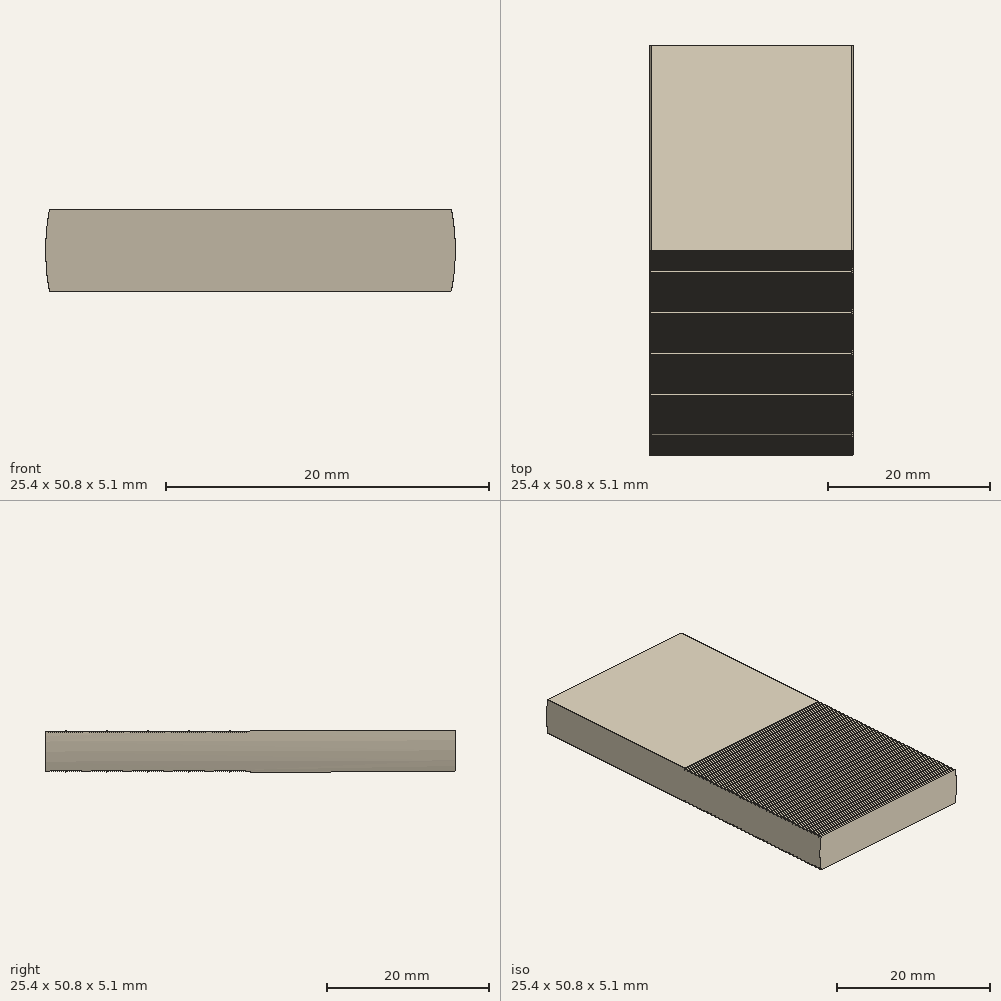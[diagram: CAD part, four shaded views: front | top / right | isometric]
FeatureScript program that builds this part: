
annotation { "Feature Type Name" : "Feature", "Feature Type Description" : "" }
export const myFeature = defineFeature(function(context is Context, id is Id, definition is map)
    precondition{}
    {
        {
            var Q0;
            Q0=qCreatedBy(makeId("Front.planeOp"),FACE);
            var sketch = newSketch(context, id + "F0", { "sketchPlane" : qUnion([Q0])});
            skCircle(sketch, "E0", {"center": v(0, 0) * mm, "radius": 12.7 * mm});
            skSolve(sketch);
        }
        {
            var Q0;
            Q0 = qSketchRegion(id + "F0", true);
            extrude(context, id + "F1", {"entities" : qUnion([Q0]), "endBound" : BoundingType.SYMMETRIC, "depth" : 50.8 * mm, "offsetDistance" : 25.4 * mm});
        }
        {
            var Q0;
            Q0=makeQuery(id+"F1.opExtrude","CAP_FACE",FACE,{"disambiguationData":[OSD([sQuery(id+"F0.wireOp",EDGE,"E0")])],"isStart":false});
            var sketch = newSketch(context, id + "F2", { "sketchPlane" : qUnion([Q0])});
            skLineSegment(sketch, "E1.bottom", {"start": v(12.45, 2.54) * mm, "end": v(-12.45, 2.54) * mm});
            skLineSegment(sketch, "E1.top", {"start": v(12.45, -2.54) * mm, "end": v(-12.45, -2.54) * mm});
            skPoint(sketch, "E1.middle", {"position": v(0, 0) * mm});
            skArc(sketch, "E2", {"start": v(-12.45, 2.54) * mm, "mid": v(-12.7, 0) * mm, "end": v(-12.45, -2.54) * mm});
            skArc(sketch, "E3.trimOffspring", {"start": v(12.45, -2.54) * mm, "mid": v(12.7, 0) * mm, "end": v(12.45, 2.54) * mm});
            skSolve(sketch);
        }
        {
            var Q0;
            Q0 = qSketchRegion(id + "F2", true);
            extrude(context, id + "F3", {"entities" : qUnion([Q0]), "operationType" : NewBodyOperationType.INTERSECT, "oppositeDirection" : true, "depth" : 50.8 * mm, "offsetDistance" : 25.4 * mm});
        }
        {
            var Q0;
            Q0=qCreatedBy(makeId("Right.planeOp"),FACE);
            var sketch = newSketch(context, id + "F4", { "sketchPlane" : qUnion([Q0])});
            skLineSegment(sketch, "E4", {"start": v(0, 2.54) * mm, "end": v(-0.13, 2.32) * mm});
            skLineSegment(sketch, "E5", {"start": v(-0.13, 2.32) * mm, "end": v(-0.25, 2.54) * mm});
            skLineSegment(sketch, "E6.1.0.0", {"start": v(-0.25, 2.54) * mm, "end": v(-0.38, 2.32) * mm});
            skLineSegment(sketch, "E6.1.0.1", {"start": v(-0.38, 2.32) * mm, "end": v(-0.5, 2.54) * mm});
            skLineSegment(sketch, "E6.2.0.0", {"start": v(-0.5, 2.54) * mm, "end": v(-0.64, 2.32) * mm});
            skLineSegment(sketch, "E6.2.0.1", {"start": v(-0.64, 2.32) * mm, "end": v(-0.76, 2.54) * mm});
            skLineSegment(sketch, "E6.3.0.0", {"start": v(-0.76, 2.54) * mm, "end": v(-0.89, 2.32) * mm});
            skLineSegment(sketch, "E6.3.0.1", {"start": v(-0.89, 2.32) * mm, "end": v(-1.02, 2.54) * mm});
            skLineSegment(sketch, "E6.4.0.0", {"start": v(-1.02, 2.54) * mm, "end": v(-1.14, 2.32) * mm});
            skLineSegment(sketch, "E6.4.0.1", {"start": v(-1.14, 2.32) * mm, "end": v(-1.27, 2.54) * mm});
            skLineSegment(sketch, "E6.5.0.0", {"start": v(-1.27, 2.54) * mm, "end": v(-1.4, 2.32) * mm});
            skLineSegment(sketch, "E6.5.0.1", {"start": v(-1.4, 2.32) * mm, "end": v(-1.52, 2.54) * mm});
            skLineSegment(sketch, "E6.6.0.0", {"start": v(-1.52, 2.54) * mm, "end": v(-1.65, 2.32) * mm});
            skLineSegment(sketch, "E6.6.0.1", {"start": v(-1.65, 2.32) * mm, "end": v(-1.78, 2.54) * mm});
            skLineSegment(sketch, "E6.7.0.0", {"start": v(-1.78, 2.54) * mm, "end": v(-1.9, 2.32) * mm});
            skLineSegment(sketch, "E6.7.0.1", {"start": v(-1.9, 2.32) * mm, "end": v(-2.03, 2.54) * mm});
            skLineSegment(sketch, "E6.8.0.0", {"start": v(-2.03, 2.54) * mm, "end": v(-2.16, 2.32) * mm});
            skLineSegment(sketch, "E6.8.0.1", {"start": v(-2.16, 2.32) * mm, "end": v(-2.29, 2.54) * mm});
            skLineSegment(sketch, "E6.9.0.0", {"start": v(-2.29, 2.54) * mm, "end": v(-2.41, 2.32) * mm});
            skLineSegment(sketch, "E6.9.0.1", {"start": v(-2.41, 2.32) * mm, "end": v(-2.54, 2.54) * mm});
            skLineSegment(sketch, "E6.10.0.0", {"start": v(-2.54, 2.54) * mm, "end": v(-2.67, 2.32) * mm});
            skLineSegment(sketch, "E6.10.0.1", {"start": v(-2.67, 2.32) * mm, "end": v(-2.8, 2.54) * mm});
            skLineSegment(sketch, "E6.11.0.0", {"start": v(-2.8, 2.54) * mm, "end": v(-2.92, 2.32) * mm});
            skLineSegment(sketch, "E6.11.0.1", {"start": v(-2.92, 2.32) * mm, "end": v(-3.05, 2.54) * mm});
            skLineSegment(sketch, "E6.12.0.0", {"start": v(-3.05, 2.54) * mm, "end": v(-3.18, 2.32) * mm});
            skLineSegment(sketch, "E6.12.0.1", {"start": v(-3.18, 2.32) * mm, "end": v(-3.3, 2.54) * mm});
            skLineSegment(sketch, "E6.13.0.0", {"start": v(-3.3, 2.54) * mm, "end": v(-3.43, 2.32) * mm});
            skLineSegment(sketch, "E6.13.0.1", {"start": v(-3.43, 2.32) * mm, "end": v(-3.56, 2.54) * mm});
            skLineSegment(sketch, "E6.14.0.0", {"start": v(-3.56, 2.54) * mm, "end": v(-3.68, 2.32) * mm});
            skLineSegment(sketch, "E6.14.0.1", {"start": v(-3.68, 2.32) * mm, "end": v(-3.81, 2.54) * mm});
            skLineSegment(sketch, "E6.15.0.0", {"start": v(-3.81, 2.54) * mm, "end": v(-3.94, 2.32) * mm});
            skLineSegment(sketch, "E6.15.0.1", {"start": v(-3.94, 2.32) * mm, "end": v(-4.06, 2.54) * mm});
            skLineSegment(sketch, "E6.16.0.0", {"start": v(-4.06, 2.54) * mm, "end": v(-4.2, 2.32) * mm});
            skLineSegment(sketch, "E6.16.0.1", {"start": v(-4.2, 2.32) * mm, "end": v(-4.32, 2.54) * mm});
            skLineSegment(sketch, "E6.17.0.0", {"start": v(-4.32, 2.54) * mm, "end": v(-4.45, 2.32) * mm});
            skLineSegment(sketch, "E6.17.0.1", {"start": v(-4.45, 2.32) * mm, "end": v(-4.57, 2.54) * mm});
            skLineSegment(sketch, "E6.18.0.0", {"start": v(-4.57, 2.54) * mm, "end": v(-4.7, 2.32) * mm});
            skLineSegment(sketch, "E6.18.0.1", {"start": v(-4.7, 2.32) * mm, "end": v(-4.83, 2.54) * mm});
            skLineSegment(sketch, "E6.19.0.0", {"start": v(-4.83, 2.54) * mm, "end": v(-4.95, 2.32) * mm});
            skLineSegment(sketch, "E6.19.0.1", {"start": v(-4.95, 2.32) * mm, "end": v(-5.08, 2.54) * mm});
            skLineSegment(sketch, "E6.20.0.0", {"start": v(-5.08, 2.54) * mm, "end": v(-5.2, 2.32) * mm});
            skLineSegment(sketch, "E6.20.0.1", {"start": v(-5.2, 2.32) * mm, "end": v(-5.33, 2.54) * mm});
            skLineSegment(sketch, "E6.21.0.0", {"start": v(-5.33, 2.54) * mm, "end": v(-5.46, 2.32) * mm});
            skLineSegment(sketch, "E6.21.0.1", {"start": v(-5.46, 2.32) * mm, "end": v(-5.59, 2.54) * mm});
            skLineSegment(sketch, "E6.22.0.0", {"start": v(-5.59, 2.54) * mm, "end": v(-5.72, 2.32) * mm});
            skLineSegment(sketch, "E6.22.0.1", {"start": v(-5.72, 2.32) * mm, "end": v(-5.84, 2.54) * mm});
            skLineSegment(sketch, "E6.23.0.0", {"start": v(-5.84, 2.54) * mm, "end": v(-5.97, 2.32) * mm});
            skLineSegment(sketch, "E6.23.0.1", {"start": v(-5.97, 2.32) * mm, "end": v(-6.1, 2.54) * mm});
            skLineSegment(sketch, "E6.24.0.0", {"start": v(-6.1, 2.54) * mm, "end": v(-6.22, 2.32) * mm});
            skLineSegment(sketch, "E6.24.0.1", {"start": v(-6.22, 2.32) * mm, "end": v(-6.35, 2.54) * mm});
            skLineSegment(sketch, "E6.25.0.0", {"start": v(-6.35, 2.54) * mm, "end": v(-6.48, 2.32) * mm});
            skLineSegment(sketch, "E6.25.0.1", {"start": v(-6.48, 2.32) * mm, "end": v(-6.6, 2.54) * mm});
            skLineSegment(sketch, "E6.26.0.0", {"start": v(-6.6, 2.54) * mm, "end": v(-6.73, 2.32) * mm});
            skLineSegment(sketch, "E6.26.0.1", {"start": v(-6.73, 2.32) * mm, "end": v(-6.86, 2.54) * mm});
            skLineSegment(sketch, "E6.27.0.0", {"start": v(-6.86, 2.54) * mm, "end": v(-6.99, 2.32) * mm});
            skLineSegment(sketch, "E6.27.0.1", {"start": v(-6.99, 2.32) * mm, "end": v(-7.11, 2.54) * mm});
            skLineSegment(sketch, "E6.28.0.0", {"start": v(-7.11, 2.54) * mm, "end": v(-7.24, 2.32) * mm});
            skLineSegment(sketch, "E6.28.0.1", {"start": v(-7.24, 2.32) * mm, "end": v(-7.37, 2.54) * mm});
            skLineSegment(sketch, "E6.29.0.0", {"start": v(-7.37, 2.54) * mm, "end": v(-7.5, 2.32) * mm});
            skLineSegment(sketch, "E6.29.0.1", {"start": v(-7.5, 2.32) * mm, "end": v(-7.62, 2.54) * mm});
            skLineSegment(sketch, "E6.30.0.0", {"start": v(-7.62, 2.54) * mm, "end": v(-7.75, 2.32) * mm});
            skLineSegment(sketch, "E6.30.0.1", {"start": v(-7.75, 2.32) * mm, "end": v(-7.87, 2.54) * mm});
            skLineSegment(sketch, "E6.31.0.0", {"start": v(-7.87, 2.54) * mm, "end": v(-8, 2.32) * mm});
            skLineSegment(sketch, "E6.31.0.1", {"start": v(-8, 2.32) * mm, "end": v(-8.13, 2.54) * mm});
            skLineSegment(sketch, "E6.32.0.0", {"start": v(-8.13, 2.54) * mm, "end": v(-8.26, 2.32) * mm});
            skLineSegment(sketch, "E6.32.0.1", {"start": v(-8.26, 2.32) * mm, "end": v(-8.38, 2.54) * mm});
            skLineSegment(sketch, "E6.33.0.0", {"start": v(-8.38, 2.54) * mm, "end": v(-8.5, 2.32) * mm});
            skLineSegment(sketch, "E6.33.0.1", {"start": v(-8.5, 2.32) * mm, "end": v(-8.64, 2.54) * mm});
            skLineSegment(sketch, "E6.34.0.0", {"start": v(-8.64, 2.54) * mm, "end": v(-8.76, 2.32) * mm});
            skLineSegment(sketch, "E6.34.0.1", {"start": v(-8.76, 2.32) * mm, "end": v(-8.9, 2.54) * mm});
            skLineSegment(sketch, "E6.35.0.0", {"start": v(-8.9, 2.54) * mm, "end": v(-9.02, 2.32) * mm});
            skLineSegment(sketch, "E6.35.0.1", {"start": v(-9.02, 2.32) * mm, "end": v(-9.14, 2.54) * mm});
            skLineSegment(sketch, "E6.36.0.0", {"start": v(-9.14, 2.54) * mm, "end": v(-9.27, 2.32) * mm});
            skLineSegment(sketch, "E6.36.0.1", {"start": v(-9.27, 2.32) * mm, "end": v(-9.4, 2.54) * mm});
            skLineSegment(sketch, "E6.37.0.0", {"start": v(-9.4, 2.54) * mm, "end": v(-9.53, 2.32) * mm});
            skLineSegment(sketch, "E6.37.0.1", {"start": v(-9.53, 2.32) * mm, "end": v(-9.65, 2.54) * mm});
            skLineSegment(sketch, "E6.38.0.0", {"start": v(-9.65, 2.54) * mm, "end": v(-9.78, 2.32) * mm});
            skLineSegment(sketch, "E6.38.0.1", {"start": v(-9.78, 2.32) * mm, "end": v(-9.9, 2.54) * mm});
            skLineSegment(sketch, "E6.39.0.0", {"start": v(-9.9, 2.54) * mm, "end": v(-10.03, 2.32) * mm});
            skLineSegment(sketch, "E6.39.0.1", {"start": v(-10.03, 2.32) * mm, "end": v(-10.16, 2.54) * mm});
            skLineSegment(sketch, "E6.40.0.0", {"start": v(-10.16, 2.54) * mm, "end": v(-10.29, 2.32) * mm});
            skLineSegment(sketch, "E6.40.0.1", {"start": v(-10.29, 2.32) * mm, "end": v(-10.41, 2.54) * mm});
            skLineSegment(sketch, "E6.41.0.0", {"start": v(-10.41, 2.54) * mm, "end": v(-10.54, 2.32) * mm});
            skLineSegment(sketch, "E6.41.0.1", {"start": v(-10.54, 2.32) * mm, "end": v(-10.67, 2.54) * mm});
            skLineSegment(sketch, "E6.42.0.0", {"start": v(-10.67, 2.54) * mm, "end": v(-10.8, 2.32) * mm});
            skLineSegment(sketch, "E6.42.0.1", {"start": v(-10.8, 2.32) * mm, "end": v(-10.92, 2.54) * mm});
            skLineSegment(sketch, "E6.43.0.0", {"start": v(-10.92, 2.54) * mm, "end": v(-11.05, 2.32) * mm});
            skLineSegment(sketch, "E6.43.0.1", {"start": v(-11.05, 2.32) * mm, "end": v(-11.18, 2.54) * mm});
            skLineSegment(sketch, "E6.44.0.0", {"start": v(-11.18, 2.54) * mm, "end": v(-11.3, 2.32) * mm});
            skLineSegment(sketch, "E6.44.0.1", {"start": v(-11.3, 2.32) * mm, "end": v(-11.43, 2.54) * mm});
            skLineSegment(sketch, "E6.45.0.0", {"start": v(-11.43, 2.54) * mm, "end": v(-11.56, 2.32) * mm});
            skLineSegment(sketch, "E6.45.0.1", {"start": v(-11.56, 2.32) * mm, "end": v(-11.68, 2.54) * mm});
            skLineSegment(sketch, "E6.46.0.0", {"start": v(-11.68, 2.54) * mm, "end": v(-11.81, 2.32) * mm});
            skLineSegment(sketch, "E6.46.0.1", {"start": v(-11.81, 2.32) * mm, "end": v(-11.94, 2.54) * mm});
            skLineSegment(sketch, "E6.47.0.0", {"start": v(-11.94, 2.54) * mm, "end": v(-12.07, 2.32) * mm});
            skLineSegment(sketch, "E6.47.0.1", {"start": v(-12.07, 2.32) * mm, "end": v(-12.2, 2.54) * mm});
            skLineSegment(sketch, "E6.48.0.0", {"start": v(-12.2, 2.54) * mm, "end": v(-12.32, 2.32) * mm});
            skLineSegment(sketch, "E6.48.0.1", {"start": v(-12.32, 2.32) * mm, "end": v(-12.45, 2.54) * mm});
            skLineSegment(sketch, "E6.49.0.0", {"start": v(-12.45, 2.54) * mm, "end": v(-12.57, 2.32) * mm});
            skLineSegment(sketch, "E6.49.0.1", {"start": v(-12.57, 2.32) * mm, "end": v(-12.7, 2.54) * mm});
            skLineSegment(sketch, "E6.50.0.0", {"start": v(-12.7, 2.54) * mm, "end": v(-12.83, 2.32) * mm});
            skLineSegment(sketch, "E6.50.0.1", {"start": v(-12.83, 2.32) * mm, "end": v(-12.95, 2.54) * mm});
            skLineSegment(sketch, "E6.51.0.0", {"start": v(-12.95, 2.54) * mm, "end": v(-13.08, 2.32) * mm});
            skLineSegment(sketch, "E6.51.0.1", {"start": v(-13.08, 2.32) * mm, "end": v(-13.2, 2.54) * mm});
            skLineSegment(sketch, "E6.52.0.0", {"start": v(-13.2, 2.54) * mm, "end": v(-13.34, 2.32) * mm});
            skLineSegment(sketch, "E6.52.0.1", {"start": v(-13.34, 2.32) * mm, "end": v(-13.46, 2.54) * mm});
            skLineSegment(sketch, "E6.53.0.0", {"start": v(-13.46, 2.54) * mm, "end": v(-13.59, 2.32) * mm});
            skLineSegment(sketch, "E6.53.0.1", {"start": v(-13.59, 2.32) * mm, "end": v(-13.72, 2.54) * mm});
            skLineSegment(sketch, "E6.54.0.0", {"start": v(-13.72, 2.54) * mm, "end": v(-13.84, 2.32) * mm});
            skLineSegment(sketch, "E6.54.0.1", {"start": v(-13.84, 2.32) * mm, "end": v(-13.97, 2.54) * mm});
            skLineSegment(sketch, "E6.55.0.0", {"start": v(-13.97, 2.54) * mm, "end": v(-14.1, 2.32) * mm});
            skLineSegment(sketch, "E6.55.0.1", {"start": v(-14.1, 2.32) * mm, "end": v(-14.22, 2.54) * mm});
            skLineSegment(sketch, "E6.56.0.0", {"start": v(-14.22, 2.54) * mm, "end": v(-14.35, 2.32) * mm});
            skLineSegment(sketch, "E6.56.0.1", {"start": v(-14.35, 2.32) * mm, "end": v(-14.48, 2.54) * mm});
            skLineSegment(sketch, "E6.57.0.0", {"start": v(-14.48, 2.54) * mm, "end": v(-14.6, 2.32) * mm});
            skLineSegment(sketch, "E6.57.0.1", {"start": v(-14.6, 2.32) * mm, "end": v(-14.73, 2.54) * mm});
            skLineSegment(sketch, "E6.58.0.0", {"start": v(-14.73, 2.54) * mm, "end": v(-14.86, 2.32) * mm});
            skLineSegment(sketch, "E6.58.0.1", {"start": v(-14.86, 2.32) * mm, "end": v(-14.99, 2.54) * mm});
            skLineSegment(sketch, "E6.59.0.0", {"start": v(-14.99, 2.54) * mm, "end": v(-15.11, 2.32) * mm});
            skLineSegment(sketch, "E6.59.0.1", {"start": v(-15.11, 2.32) * mm, "end": v(-15.24, 2.54) * mm});
            skLineSegment(sketch, "E6.60.0.0", {"start": v(-15.24, 2.54) * mm, "end": v(-15.37, 2.32) * mm});
            skLineSegment(sketch, "E6.60.0.1", {"start": v(-15.37, 2.32) * mm, "end": v(-15.5, 2.54) * mm});
            skLineSegment(sketch, "E6.61.0.0", {"start": v(-15.5, 2.54) * mm, "end": v(-15.62, 2.32) * mm});
            skLineSegment(sketch, "E6.61.0.1", {"start": v(-15.62, 2.32) * mm, "end": v(-15.75, 2.54) * mm});
            skLineSegment(sketch, "E6.62.0.0", {"start": v(-15.75, 2.54) * mm, "end": v(-15.88, 2.32) * mm});
            skLineSegment(sketch, "E6.62.0.1", {"start": v(-15.88, 2.32) * mm, "end": v(-16, 2.54) * mm});
            skLineSegment(sketch, "E6.63.0.0", {"start": v(-16, 2.54) * mm, "end": v(-16.13, 2.32) * mm});
            skLineSegment(sketch, "E6.63.0.1", {"start": v(-16.13, 2.32) * mm, "end": v(-16.26, 2.54) * mm});
            skLineSegment(sketch, "E6.64.0.0", {"start": v(-16.26, 2.54) * mm, "end": v(-16.38, 2.32) * mm});
            skLineSegment(sketch, "E6.64.0.1", {"start": v(-16.38, 2.32) * mm, "end": v(-16.51, 2.54) * mm});
            skLineSegment(sketch, "E6.65.0.0", {"start": v(-16.51, 2.54) * mm, "end": v(-16.64, 2.32) * mm});
            skLineSegment(sketch, "E6.65.0.1", {"start": v(-16.64, 2.32) * mm, "end": v(-16.76, 2.54) * mm});
            skLineSegment(sketch, "E6.66.0.0", {"start": v(-16.76, 2.54) * mm, "end": v(-16.9, 2.32) * mm});
            skLineSegment(sketch, "E6.66.0.1", {"start": v(-16.9, 2.32) * mm, "end": v(-17.02, 2.54) * mm});
            skLineSegment(sketch, "E6.67.0.0", {"start": v(-17.02, 2.54) * mm, "end": v(-17.15, 2.32) * mm});
            skLineSegment(sketch, "E6.67.0.1", {"start": v(-17.15, 2.32) * mm, "end": v(-17.27, 2.54) * mm});
            skLineSegment(sketch, "E6.68.0.0", {"start": v(-17.27, 2.54) * mm, "end": v(-17.4, 2.32) * mm});
            skLineSegment(sketch, "E6.68.0.1", {"start": v(-17.4, 2.32) * mm, "end": v(-17.53, 2.54) * mm});
            skLineSegment(sketch, "E6.69.0.0", {"start": v(-17.53, 2.54) * mm, "end": v(-17.65, 2.32) * mm});
            skLineSegment(sketch, "E6.69.0.1", {"start": v(-17.65, 2.32) * mm, "end": v(-17.78, 2.54) * mm});
            skLineSegment(sketch, "E6.70.0.0", {"start": v(-17.78, 2.54) * mm, "end": v(-17.9, 2.32) * mm});
            skLineSegment(sketch, "E6.70.0.1", {"start": v(-17.9, 2.32) * mm, "end": v(-18.03, 2.54) * mm});
            skLineSegment(sketch, "E6.71.0.0", {"start": v(-18.03, 2.54) * mm, "end": v(-18.16, 2.32) * mm});
            skLineSegment(sketch, "E6.71.0.1", {"start": v(-18.16, 2.32) * mm, "end": v(-18.29, 2.54) * mm});
            skLineSegment(sketch, "E6.72.0.0", {"start": v(-18.29, 2.54) * mm, "end": v(-18.42, 2.32) * mm});
            skLineSegment(sketch, "E6.72.0.1", {"start": v(-18.42, 2.32) * mm, "end": v(-18.54, 2.54) * mm});
            skLineSegment(sketch, "E6.73.0.0", {"start": v(-18.54, 2.54) * mm, "end": v(-18.67, 2.32) * mm});
            skLineSegment(sketch, "E6.73.0.1", {"start": v(-18.67, 2.32) * mm, "end": v(-18.8, 2.54) * mm});
            skLineSegment(sketch, "E6.74.0.0", {"start": v(-18.8, 2.54) * mm, "end": v(-18.92, 2.32) * mm});
            skLineSegment(sketch, "E6.74.0.1", {"start": v(-18.92, 2.32) * mm, "end": v(-19.05, 2.54) * mm});
            skLineSegment(sketch, "E6.75.0.0", {"start": v(-19.05, 2.54) * mm, "end": v(-19.18, 2.32) * mm});
            skLineSegment(sketch, "E6.75.0.1", {"start": v(-19.18, 2.32) * mm, "end": v(-19.3, 2.54) * mm});
            skLineSegment(sketch, "E6.76.0.0", {"start": v(-19.3, 2.54) * mm, "end": v(-19.43, 2.32) * mm});
            skLineSegment(sketch, "E6.76.0.1", {"start": v(-19.43, 2.32) * mm, "end": v(-19.56, 2.54) * mm});
            skLineSegment(sketch, "E6.77.0.0", {"start": v(-19.56, 2.54) * mm, "end": v(-19.69, 2.32) * mm});
            skLineSegment(sketch, "E6.77.0.1", {"start": v(-19.69, 2.32) * mm, "end": v(-19.81, 2.54) * mm});
            skLineSegment(sketch, "E6.78.0.0", {"start": v(-19.81, 2.54) * mm, "end": v(-19.94, 2.32) * mm});
            skLineSegment(sketch, "E6.78.0.1", {"start": v(-19.94, 2.32) * mm, "end": v(-20.07, 2.54) * mm});
            skLineSegment(sketch, "E6.79.0.0", {"start": v(-20.07, 2.54) * mm, "end": v(-20.2, 2.32) * mm});
            skLineSegment(sketch, "E6.79.0.1", {"start": v(-20.2, 2.32) * mm, "end": v(-20.32, 2.54) * mm});
            skLineSegment(sketch, "E6.80.0.0", {"start": v(-20.32, 2.54) * mm, "end": v(-20.45, 2.32) * mm});
            skLineSegment(sketch, "E6.80.0.1", {"start": v(-20.45, 2.32) * mm, "end": v(-20.57, 2.54) * mm});
            skLineSegment(sketch, "E6.81.0.0", {"start": v(-20.57, 2.54) * mm, "end": v(-20.7, 2.32) * mm});
            skLineSegment(sketch, "E6.81.0.1", {"start": v(-20.7, 2.32) * mm, "end": v(-20.83, 2.54) * mm});
            skLineSegment(sketch, "E6.82.0.0", {"start": v(-20.83, 2.54) * mm, "end": v(-20.96, 2.32) * mm});
            skLineSegment(sketch, "E6.82.0.1", {"start": v(-20.96, 2.32) * mm, "end": v(-21.08, 2.54) * mm});
            skLineSegment(sketch, "E6.83.0.0", {"start": v(-21.08, 2.54) * mm, "end": v(-21.2, 2.32) * mm});
            skLineSegment(sketch, "E6.83.0.1", {"start": v(-21.2, 2.32) * mm, "end": v(-21.34, 2.54) * mm});
            skLineSegment(sketch, "E6.84.0.0", {"start": v(-21.34, 2.54) * mm, "end": v(-21.46, 2.32) * mm});
            skLineSegment(sketch, "E6.84.0.1", {"start": v(-21.46, 2.32) * mm, "end": v(-21.6, 2.54) * mm});
            skLineSegment(sketch, "E6.85.0.0", {"start": v(-21.6, 2.54) * mm, "end": v(-21.72, 2.32) * mm});
            skLineSegment(sketch, "E6.85.0.1", {"start": v(-21.72, 2.32) * mm, "end": v(-21.84, 2.54) * mm});
            skLineSegment(sketch, "E6.86.0.0", {"start": v(-21.84, 2.54) * mm, "end": v(-21.97, 2.32) * mm});
            skLineSegment(sketch, "E6.86.0.1", {"start": v(-21.97, 2.32) * mm, "end": v(-22.1, 2.54) * mm});
            skLineSegment(sketch, "E6.87.0.0", {"start": v(-22.1, 2.54) * mm, "end": v(-22.23, 2.32) * mm});
            skLineSegment(sketch, "E6.87.0.1", {"start": v(-22.23, 2.32) * mm, "end": v(-22.35, 2.54) * mm});
            skLineSegment(sketch, "E6.88.0.0", {"start": v(-22.35, 2.54) * mm, "end": v(-22.48, 2.32) * mm});
            skLineSegment(sketch, "E6.88.0.1", {"start": v(-22.48, 2.32) * mm, "end": v(-22.6, 2.54) * mm});
            skLineSegment(sketch, "E6.89.0.0", {"start": v(-22.6, 2.54) * mm, "end": v(-22.73, 2.32) * mm});
            skLineSegment(sketch, "E6.89.0.1", {"start": v(-22.73, 2.32) * mm, "end": v(-22.86, 2.54) * mm});
            skLineSegment(sketch, "E6.90.0.0", {"start": v(-22.86, 2.54) * mm, "end": v(-22.99, 2.32) * mm});
            skLineSegment(sketch, "E6.90.0.1", {"start": v(-22.99, 2.32) * mm, "end": v(-23.11, 2.54) * mm});
            skLineSegment(sketch, "E6.91.0.0", {"start": v(-23.11, 2.54) * mm, "end": v(-23.24, 2.32) * mm});
            skLineSegment(sketch, "E6.91.0.1", {"start": v(-23.24, 2.32) * mm, "end": v(-23.37, 2.54) * mm});
            skLineSegment(sketch, "E6.92.0.0", {"start": v(-23.37, 2.54) * mm, "end": v(-23.5, 2.32) * mm});
            skLineSegment(sketch, "E6.92.0.1", {"start": v(-23.5, 2.32) * mm, "end": v(-23.62, 2.54) * mm});
            skLineSegment(sketch, "E6.93.0.0", {"start": v(-23.62, 2.54) * mm, "end": v(-23.75, 2.32) * mm});
            skLineSegment(sketch, "E6.93.0.1", {"start": v(-23.75, 2.32) * mm, "end": v(-23.88, 2.54) * mm});
            skLineSegment(sketch, "E6.94.0.0", {"start": v(-23.88, 2.54) * mm, "end": v(-24, 2.32) * mm});
            skLineSegment(sketch, "E6.94.0.1", {"start": v(-24, 2.32) * mm, "end": v(-24.13, 2.54) * mm});
            skLineSegment(sketch, "E6.95.0.0", {"start": v(-24.13, 2.54) * mm, "end": v(-24.26, 2.32) * mm});
            skLineSegment(sketch, "E6.95.0.1", {"start": v(-24.26, 2.32) * mm, "end": v(-24.38, 2.54) * mm});
            skLineSegment(sketch, "E6.96.0.0", {"start": v(-24.38, 2.54) * mm, "end": v(-24.51, 2.32) * mm});
            skLineSegment(sketch, "E6.96.0.1", {"start": v(-24.51, 2.32) * mm, "end": v(-24.64, 2.54) * mm});
            skLineSegment(sketch, "E6.97.0.0", {"start": v(-24.64, 2.54) * mm, "end": v(-24.77, 2.32) * mm});
            skLineSegment(sketch, "E6.97.0.1", {"start": v(-24.77, 2.32) * mm, "end": v(-24.9, 2.54) * mm});
            skLineSegment(sketch, "E6.98.0.0", {"start": v(-24.9, 2.54) * mm, "end": v(-25.02, 2.32) * mm});
            skLineSegment(sketch, "E6.98.0.1", {"start": v(-25.02, 2.32) * mm, "end": v(-25.15, 2.54) * mm});
            skLineSegment(sketch, "E6.99.0.0", {"start": v(-25.15, 2.54) * mm, "end": v(-25.27, 2.32) * mm});
            skLineSegment(sketch, "E6.99.0.1", {"start": v(-25.27, 2.32) * mm, "end": v(-25.4, 2.54) * mm});
            skLineSegment(sketch, "E6.direction1", {"start": v(-0.13, -2.33) * mm, "end": v(-0.38, -2.33) * mm, "construction": true});
            skLineSegment(sketch, "E7", {"start": v(0, 2.54) * mm, "end": v(0, 2.6) * mm});
            skLineSegment(sketch, "E8", {"start": v(0, 2.6) * mm, "end": v(-25.4, 2.6) * mm});
            skLineSegment(sketch, "E9", {"start": v(-25.4, 2.6) * mm, "end": v(-25.4, 2.54) * mm});
            skLineSegment(sketch, "E10.MirrorCS", {"start": v(-0.13, -2.33) * mm, "end": v(-0.25, -2.55) * mm});
            skLineSegment(sketch, "E11.MirrorCS", {"start": v(0, -2.55) * mm, "end": v(-0.13, -2.33) * mm});
            skLineSegment(sketch, "E12.MirrorCS", {"start": v(-0.38, -2.33) * mm, "end": v(-0.5, -2.55) * mm});
            skLineSegment(sketch, "E13.MirrorCS", {"start": v(-25.4, -2.6) * mm, "end": v(-25.4, -2.55) * mm});
            skLineSegment(sketch, "E14.MirrorCS", {"start": v(-0.25, -2.55) * mm, "end": v(-0.38, -2.33) * mm});
            skLineSegment(sketch, "E15.MirrorCS", {"start": v(0, -2.55) * mm, "end": v(0, -2.6) * mm});
            skLineSegment(sketch, "E16.MirrorCS", {"start": v(-17.4, -2.33) * mm, "end": v(-17.53, -2.55) * mm});
            skLineSegment(sketch, "E17.MirrorCS", {"start": v(-1.52, -2.55) * mm, "end": v(-1.65, -2.33) * mm});
            skLineSegment(sketch, "E18.MirrorCS", {"start": v(-8.64, -2.55) * mm, "end": v(-8.76, -2.33) * mm});
            skLineSegment(sketch, "E19.MirrorCS", {"start": v(-24.9, -2.55) * mm, "end": v(-25.02, -2.33) * mm});
            skLineSegment(sketch, "E20.MirrorCS", {"start": v(-20.83, -2.55) * mm, "end": v(-20.96, -2.33) * mm});
            skLineSegment(sketch, "E21.MirrorCS", {"start": v(-23.11, -2.55) * mm, "end": v(-23.24, -2.33) * mm});
            skLineSegment(sketch, "E22.MirrorCS", {"start": v(-6.99, -2.33) * mm, "end": v(-7.11, -2.55) * mm});
            skLineSegment(sketch, "E23.MirrorCS", {"start": v(-15.11, -2.33) * mm, "end": v(-15.24, -2.55) * mm});
            skLineSegment(sketch, "E24.MirrorCS", {"start": v(-9.02, -2.33) * mm, "end": v(-9.14, -2.55) * mm});
            skLineSegment(sketch, "E25.MirrorCS", {"start": v(-21.46, -2.33) * mm, "end": v(-21.6, -2.55) * mm});
            skLineSegment(sketch, "E26.MirrorCS", {"start": v(-4.06, -2.55) * mm, "end": v(-4.2, -2.33) * mm});
            skLineSegment(sketch, "E27.MirrorCS", {"start": v(-21.34, -2.55) * mm, "end": v(-21.46, -2.33) * mm});
            skLineSegment(sketch, "E28.MirrorCS", {"start": v(-18.03, -2.55) * mm, "end": v(-18.16, -2.33) * mm});
            skLineSegment(sketch, "E29.MirrorCS", {"start": v(-3.56, -2.55) * mm, "end": v(-3.68, -2.33) * mm});
            skLineSegment(sketch, "E30.MirrorCS", {"start": v(-4.32, -2.55) * mm, "end": v(-4.45, -2.33) * mm});
            skLineSegment(sketch, "E31.MirrorCS", {"start": v(-9.78, -2.33) * mm, "end": v(-9.9, -2.55) * mm});
            skLineSegment(sketch, "E32.MirrorCS", {"start": v(-8.5, -2.33) * mm, "end": v(-8.64, -2.55) * mm});
            skLineSegment(sketch, "E33.MirrorCS", {"start": v(-20.7, -2.33) * mm, "end": v(-20.83, -2.55) * mm});
            skLineSegment(sketch, "E34.MirrorCS", {"start": v(-19.05, -2.55) * mm, "end": v(-19.18, -2.33) * mm});
            skLineSegment(sketch, "E35.MirrorCS", {"start": v(-14.73, -2.55) * mm, "end": v(-14.86, -2.33) * mm});
            skLineSegment(sketch, "E36.MirrorCS", {"start": v(-17.9, -2.33) * mm, "end": v(-18.03, -2.55) * mm});
            skLineSegment(sketch, "E37.MirrorCS", {"start": v(-24, -2.33) * mm, "end": v(-24.13, -2.55) * mm});
            skLineSegment(sketch, "E38.MirrorCS", {"start": v(-18.67, -2.33) * mm, "end": v(-18.8, -2.55) * mm});
            skLineSegment(sketch, "E39.MirrorCS", {"start": v(-4.2, -2.33) * mm, "end": v(-4.32, -2.55) * mm});
            skLineSegment(sketch, "E40.MirrorCS", {"start": v(-9.14, -2.55) * mm, "end": v(-9.27, -2.33) * mm});
            skLineSegment(sketch, "E41.MirrorCS", {"start": v(-10.92, -2.55) * mm, "end": v(-11.05, -2.33) * mm});
            skLineSegment(sketch, "E42.MirrorCS", {"start": v(-7.37, -2.55) * mm, "end": v(-7.5, -2.33) * mm});
            skLineSegment(sketch, "E43.MirrorCS", {"start": v(-1.4, -2.33) * mm, "end": v(-1.52, -2.55) * mm});
            skLineSegment(sketch, "E44.MirrorCS", {"start": v(-1.27, -2.55) * mm, "end": v(-1.4, -2.33) * mm});
            skLineSegment(sketch, "E45.MirrorCS", {"start": v(-19.81, -2.55) * mm, "end": v(-19.94, -2.33) * mm});
            skLineSegment(sketch, "E46.MirrorCS", {"start": v(-19.43, -2.33) * mm, "end": v(-19.56, -2.55) * mm});
            skLineSegment(sketch, "E47.MirrorCS", {"start": v(-11.94, -2.55) * mm, "end": v(-12.07, -2.33) * mm});
            skLineSegment(sketch, "E48.MirrorCS", {"start": v(-11.68, -2.55) * mm, "end": v(-11.81, -2.33) * mm});
            skLineSegment(sketch, "E49.MirrorCS", {"start": v(-1.9, -2.33) * mm, "end": v(-2.03, -2.55) * mm});
            skLineSegment(sketch, "E50.MirrorCS", {"start": v(-9.9, -2.55) * mm, "end": v(-10.03, -2.33) * mm});
            skLineSegment(sketch, "E51.MirrorCS", {"start": v(-21.6, -2.55) * mm, "end": v(-21.72, -2.33) * mm});
            skLineSegment(sketch, "E52.MirrorCS", {"start": v(-13.34, -2.33) * mm, "end": v(-13.46, -2.55) * mm});
            skLineSegment(sketch, "E53.MirrorCS", {"start": v(-8.9, -2.55) * mm, "end": v(-9.02, -2.33) * mm});
            skLineSegment(sketch, "E54.MirrorCS", {"start": v(-18.8, -2.55) * mm, "end": v(-18.92, -2.33) * mm});
            skLineSegment(sketch, "E55.MirrorCS", {"start": v(-23.24, -2.33) * mm, "end": v(-23.37, -2.55) * mm});
            skLineSegment(sketch, "E56.MirrorCS", {"start": v(-9.4, -2.55) * mm, "end": v(-9.53, -2.33) * mm});
            skLineSegment(sketch, "E57.MirrorCS", {"start": v(-2.54, -2.55) * mm, "end": v(-2.67, -2.33) * mm});
            skLineSegment(sketch, "E58.MirrorCS", {"start": v(-17.02, -2.55) * mm, "end": v(-17.15, -2.33) * mm});
            skLineSegment(sketch, "E59.MirrorCS", {"start": v(-20.57, -2.55) * mm, "end": v(-20.7, -2.33) * mm});
            skLineSegment(sketch, "E60.MirrorCS", {"start": v(-10.29, -2.33) * mm, "end": v(-10.41, -2.55) * mm});
            skLineSegment(sketch, "E61.MirrorCS", {"start": v(-20.45, -2.33) * mm, "end": v(-20.57, -2.55) * mm});
            skLineSegment(sketch, "E62.MirrorCS", {"start": v(-21.84, -2.55) * mm, "end": v(-21.97, -2.33) * mm});
            skLineSegment(sketch, "E63.MirrorCS", {"start": v(-3.3, -2.55) * mm, "end": v(-3.43, -2.33) * mm});
            skLineSegment(sketch, "E64.MirrorCS", {"start": v(-16.38, -2.33) * mm, "end": v(-16.51, -2.55) * mm});
            skLineSegment(sketch, "E65.MirrorCS", {"start": v(-0.5, -2.55) * mm, "end": v(-0.64, -2.33) * mm});
            skLineSegment(sketch, "E66.MirrorCS", {"start": v(-2.67, -2.33) * mm, "end": v(-2.8, -2.55) * mm});
            skLineSegment(sketch, "E67.MirrorCS", {"start": v(-23.88, -2.55) * mm, "end": v(-24, -2.33) * mm});
            skLineSegment(sketch, "E68.MirrorCS", {"start": v(-4.7, -2.33) * mm, "end": v(-4.83, -2.55) * mm});
            skLineSegment(sketch, "E69.MirrorCS", {"start": v(-23.5, -2.33) * mm, "end": v(-23.62, -2.55) * mm});
            skLineSegment(sketch, "E70.MirrorCS", {"start": v(-22.86, -2.55) * mm, "end": v(-22.99, -2.33) * mm});
            skLineSegment(sketch, "E71.MirrorCS", {"start": v(-6.86, -2.55) * mm, "end": v(-6.99, -2.33) * mm});
            skLineSegment(sketch, "E72.MirrorCS", {"start": v(-8.13, -2.55) * mm, "end": v(-8.26, -2.33) * mm});
            skLineSegment(sketch, "E73.MirrorCS", {"start": v(-3.43, -2.33) * mm, "end": v(-3.56, -2.55) * mm});
            skLineSegment(sketch, "E74.MirrorCS", {"start": v(-4.57, -2.55) * mm, "end": v(-4.7, -2.33) * mm});
            skLineSegment(sketch, "E75.MirrorCS", {"start": v(-18.29, -2.55) * mm, "end": v(-18.42, -2.33) * mm});
            skLineSegment(sketch, "E76.MirrorCS", {"start": v(-14.35, -2.33) * mm, "end": v(-14.48, -2.55) * mm});
            skLineSegment(sketch, "E77.MirrorCS", {"start": v(-12.32, -2.33) * mm, "end": v(-12.45, -2.55) * mm});
            skLineSegment(sketch, "E78.MirrorCS", {"start": v(-16.13, -2.33) * mm, "end": v(-16.26, -2.55) * mm});
            skLineSegment(sketch, "E79.MirrorCS", {"start": v(-3.05, -2.55) * mm, "end": v(-3.18, -2.33) * mm});
            skLineSegment(sketch, "E80.MirrorCS", {"start": v(-1.65, -2.33) * mm, "end": v(-1.78, -2.55) * mm});
            skLineSegment(sketch, "E81.MirrorCS", {"start": v(-14.86, -2.33) * mm, "end": v(-14.99, -2.55) * mm});
            skLineSegment(sketch, "E82.MirrorCS", {"start": v(-5.2, -2.33) * mm, "end": v(-5.33, -2.55) * mm});
            skLineSegment(sketch, "E83.MirrorCS", {"start": v(-11.43, -2.55) * mm, "end": v(-11.56, -2.33) * mm});
            skLineSegment(sketch, "E84.MirrorCS", {"start": v(-2.41, -2.33) * mm, "end": v(-2.54, -2.55) * mm});
            skLineSegment(sketch, "E85.MirrorCS", {"start": v(-19.3, -2.55) * mm, "end": v(-19.43, -2.33) * mm});
            skLineSegment(sketch, "E86.MirrorCS", {"start": v(-10.03, -2.33) * mm, "end": v(-10.16, -2.55) * mm});
            skLineSegment(sketch, "E87.MirrorCS", {"start": v(-22.73, -2.33) * mm, "end": v(-22.86, -2.55) * mm});
            skLineSegment(sketch, "E88.MirrorCS", {"start": v(-8.76, -2.33) * mm, "end": v(-8.9, -2.55) * mm});
            skLineSegment(sketch, "E89.MirrorCS", {"start": v(-8.26, -2.33) * mm, "end": v(-8.38, -2.55) * mm});
            skLineSegment(sketch, "E90.MirrorCS", {"start": v(-16.9, -2.33) * mm, "end": v(-17.02, -2.55) * mm});
            skLineSegment(sketch, "E91.MirrorCS", {"start": v(-9.65, -2.55) * mm, "end": v(-9.78, -2.33) * mm});
            skLineSegment(sketch, "E92.MirrorCS", {"start": v(-6.1, -2.55) * mm, "end": v(-6.22, -2.33) * mm});
            skLineSegment(sketch, "E93.MirrorCS", {"start": v(-9.27, -2.33) * mm, "end": v(-9.4, -2.55) * mm});
            skLineSegment(sketch, "E94.MirrorCS", {"start": v(-9.53, -2.33) * mm, "end": v(-9.65, -2.55) * mm});
            skLineSegment(sketch, "E95.MirrorCS", {"start": v(-5.46, -2.33) * mm, "end": v(-5.59, -2.55) * mm});
            skLineSegment(sketch, "E96.MirrorCS", {"start": v(-12.57, -2.33) * mm, "end": v(-12.7, -2.55) * mm});
            skLineSegment(sketch, "E97.MirrorCS", {"start": v(-21.97, -2.33) * mm, "end": v(-22.1, -2.55) * mm});
            skLineSegment(sketch, "E98.MirrorCS", {"start": v(-20.32, -2.55) * mm, "end": v(-20.45, -2.33) * mm});
            skLineSegment(sketch, "E99.MirrorCS", {"start": v(-22.99, -2.33) * mm, "end": v(-23.11, -2.55) * mm});
            skLineSegment(sketch, "E100.MirrorCS", {"start": v(-21.72, -2.33) * mm, "end": v(-21.84, -2.55) * mm});
            skLineSegment(sketch, "E101.MirrorCS", {"start": v(-17.65, -2.33) * mm, "end": v(-17.78, -2.55) * mm});
            skLineSegment(sketch, "E102.MirrorCS", {"start": v(-12.7, -2.55) * mm, "end": v(-12.83, -2.33) * mm});
            skLineSegment(sketch, "E103.MirrorCS", {"start": v(-13.59, -2.33) * mm, "end": v(-13.72, -2.55) * mm});
            skLineSegment(sketch, "E104.MirrorCS", {"start": v(-3.18, -2.33) * mm, "end": v(-3.3, -2.55) * mm});
            skLineSegment(sketch, "E105.MirrorCS", {"start": v(-17.15, -2.33) * mm, "end": v(-17.27, -2.55) * mm});
            skLineSegment(sketch, "E106.MirrorCS", {"start": v(-14.99, -2.55) * mm, "end": v(-15.11, -2.33) * mm});
            skLineSegment(sketch, "E107.MirrorCS", {"start": v(-18.16, -2.33) * mm, "end": v(-18.29, -2.55) * mm});
            skLineSegment(sketch, "E108.MirrorCS", {"start": v(-14.1, -2.33) * mm, "end": v(-14.22, -2.55) * mm});
            skLineSegment(sketch, "E109.MirrorCS", {"start": v(-23.37, -2.55) * mm, "end": v(-23.5, -2.33) * mm});
            skLineSegment(sketch, "E110.MirrorCS", {"start": v(-2.16, -2.33) * mm, "end": v(-2.29, -2.55) * mm});
            skLineSegment(sketch, "E111.MirrorCS", {"start": v(-19.18, -2.33) * mm, "end": v(-19.3, -2.55) * mm});
            skLineSegment(sketch, "E112.MirrorCS", {"start": v(-15.75, -2.55) * mm, "end": v(-15.88, -2.33) * mm});
            skLineSegment(sketch, "E113.MirrorCS", {"start": v(-14.48, -2.55) * mm, "end": v(-14.6, -2.33) * mm});
            skLineSegment(sketch, "E114.MirrorCS", {"start": v(-24.38, -2.55) * mm, "end": v(-24.51, -2.33) * mm});
            skLineSegment(sketch, "E115.MirrorCS", {"start": v(-22.23, -2.33) * mm, "end": v(-22.35, -2.55) * mm});
            skLineSegment(sketch, "E116.MirrorCS", {"start": v(-16.76, -2.55) * mm, "end": v(-16.9, -2.33) * mm});
            skLineSegment(sketch, "E117.MirrorCS", {"start": v(-10.8, -2.33) * mm, "end": v(-10.92, -2.55) * mm});
            skLineSegment(sketch, "E118.MirrorCS", {"start": v(-10.16, -2.55) * mm, "end": v(-10.29, -2.33) * mm});
            skLineSegment(sketch, "E119.MirrorCS", {"start": v(-15.37, -2.33) * mm, "end": v(-15.5, -2.55) * mm});
            skLineSegment(sketch, "E120.MirrorCS", {"start": v(-11.05, -2.33) * mm, "end": v(-11.18, -2.55) * mm});
            skLineSegment(sketch, "E121.MirrorCS", {"start": v(-6.48, -2.33) * mm, "end": v(-6.6, -2.55) * mm});
            skLineSegment(sketch, "E122.MirrorCS", {"start": v(-15.88, -2.33) * mm, "end": v(-16, -2.55) * mm});
            skLineSegment(sketch, "E123.MirrorCS", {"start": v(-5.59, -2.55) * mm, "end": v(-5.72, -2.33) * mm});
            skLineSegment(sketch, "E124.MirrorCS", {"start": v(-7.5, -2.33) * mm, "end": v(-7.62, -2.55) * mm});
            skLineSegment(sketch, "E125.MirrorCS", {"start": v(-5.97, -2.33) * mm, "end": v(-6.1, -2.55) * mm});
            skLineSegment(sketch, "E126.MirrorCS", {"start": v(-24.51, -2.33) * mm, "end": v(-24.64, -2.55) * mm});
            skLineSegment(sketch, "E127.MirrorCS", {"start": v(-15.5, -2.55) * mm, "end": v(-15.62, -2.33) * mm});
            skLineSegment(sketch, "E128.MirrorCS", {"start": v(-13.84, -2.33) * mm, "end": v(-13.97, -2.55) * mm});
            skLineSegment(sketch, "E129.MirrorCS", {"start": v(-13.08, -2.33) * mm, "end": v(-13.2, -2.55) * mm});
            skLineSegment(sketch, "E130.MirrorCS", {"start": v(-1.78, -2.55) * mm, "end": v(-1.9, -2.33) * mm});
            skLineSegment(sketch, "E131.MirrorCS", {"start": v(-4.45, -2.33) * mm, "end": v(-4.57, -2.55) * mm});
            skLineSegment(sketch, "E132.MirrorCS", {"start": v(-17.78, -2.55) * mm, "end": v(-17.9, -2.33) * mm});
            skLineSegment(sketch, "E133.MirrorCS", {"start": v(-20.96, -2.33) * mm, "end": v(-21.08, -2.55) * mm});
            skLineSegment(sketch, "E134.MirrorCS", {"start": v(-4.83, -2.55) * mm, "end": v(-4.95, -2.33) * mm});
            skLineSegment(sketch, "E135.MirrorCS", {"start": v(-2.8, -2.55) * mm, "end": v(-2.92, -2.33) * mm});
            skLineSegment(sketch, "E136.MirrorCS", {"start": v(-18.54, -2.55) * mm, "end": v(-18.67, -2.33) * mm});
            skLineSegment(sketch, "E137.MirrorCS", {"start": v(-18.92, -2.33) * mm, "end": v(-19.05, -2.55) * mm});
            skLineSegment(sketch, "E138.MirrorCS", {"start": v(-7.11, -2.55) * mm, "end": v(-7.24, -2.33) * mm});
            skLineSegment(sketch, "E139.MirrorCS", {"start": v(-6.35, -2.55) * mm, "end": v(-6.48, -2.33) * mm});
            skLineSegment(sketch, "E140.MirrorCS", {"start": v(-3.68, -2.33) * mm, "end": v(-3.81, -2.55) * mm});
            skLineSegment(sketch, "E141.MirrorCS", {"start": v(-0.89, -2.33) * mm, "end": v(-1.02, -2.55) * mm});
            skLineSegment(sketch, "E142.MirrorCS", {"start": v(-19.69, -2.33) * mm, "end": v(-19.81, -2.55) * mm});
            skLineSegment(sketch, "E143.MirrorCS", {"start": v(-5.33, -2.55) * mm, "end": v(-5.46, -2.33) * mm});
            skLineSegment(sketch, "E144.MirrorCS", {"start": v(-8, -2.33) * mm, "end": v(-8.13, -2.55) * mm});
            skLineSegment(sketch, "E145.MirrorCS", {"start": v(-15.24, -2.55) * mm, "end": v(-15.37, -2.33) * mm});
            skLineSegment(sketch, "E146.MirrorCS", {"start": v(-24.77, -2.33) * mm, "end": v(-24.9, -2.55) * mm});
            skLineSegment(sketch, "E147.MirrorCS", {"start": v(-25.15, -2.55) * mm, "end": v(-25.27, -2.33) * mm});
            skLineSegment(sketch, "E148.MirrorCS", {"start": v(-3.94, -2.33) * mm, "end": v(-4.06, -2.55) * mm});
            skLineSegment(sketch, "E149.MirrorCS", {"start": v(-15.62, -2.33) * mm, "end": v(-15.75, -2.55) * mm});
            skLineSegment(sketch, "E150.MirrorCS", {"start": v(-1.14, -2.33) * mm, "end": v(-1.27, -2.55) * mm});
            skLineSegment(sketch, "E151.MirrorCS", {"start": v(-16.26, -2.55) * mm, "end": v(-16.38, -2.33) * mm});
            skLineSegment(sketch, "E152.MirrorCS", {"start": v(-5.08, -2.55) * mm, "end": v(-5.2, -2.33) * mm});
            skLineSegment(sketch, "E153.MirrorCS", {"start": v(-22.6, -2.55) * mm, "end": v(-22.73, -2.33) * mm});
            skLineSegment(sketch, "E154.MirrorCS", {"start": v(-2.92, -2.33) * mm, "end": v(-3.05, -2.55) * mm});
            skLineSegment(sketch, "E155.MirrorCS", {"start": v(-16.64, -2.33) * mm, "end": v(-16.76, -2.55) * mm});
            skLineSegment(sketch, "E156.MirrorCS", {"start": v(-21.2, -2.33) * mm, "end": v(-21.34, -2.55) * mm});
            skLineSegment(sketch, "E157.MirrorCS", {"start": v(-12.2, -2.55) * mm, "end": v(-12.32, -2.33) * mm});
            skLineSegment(sketch, "E158.MirrorCS", {"start": v(-4.95, -2.33) * mm, "end": v(-5.08, -2.55) * mm});
            skLineSegment(sketch, "E159.MirrorCS", {"start": v(-2.29, -2.55) * mm, "end": v(-2.41, -2.33) * mm});
            skLineSegment(sketch, "E160.MirrorCS", {"start": v(-23.62, -2.55) * mm, "end": v(-23.75, -2.33) * mm});
            skLineSegment(sketch, "E161.MirrorCS", {"start": v(-20.2, -2.33) * mm, "end": v(-20.32, -2.55) * mm});
            skLineSegment(sketch, "E162.MirrorCS", {"start": v(-1.02, -2.55) * mm, "end": v(-1.14, -2.33) * mm});
            skLineSegment(sketch, "E163.MirrorCS", {"start": v(-13.72, -2.55) * mm, "end": v(-13.84, -2.33) * mm});
            skLineSegment(sketch, "E164.MirrorCS", {"start": v(-19.94, -2.33) * mm, "end": v(-20.07, -2.55) * mm});
            skLineSegment(sketch, "E165.MirrorCS", {"start": v(-22.1, -2.55) * mm, "end": v(-22.23, -2.33) * mm});
            skLineSegment(sketch, "E166.MirrorCS", {"start": v(-12.83, -2.33) * mm, "end": v(-12.95, -2.55) * mm});
            skLineSegment(sketch, "E167.MirrorCS", {"start": v(-13.46, -2.55) * mm, "end": v(-13.59, -2.33) * mm});
            skLineSegment(sketch, "E168.MirrorCS", {"start": v(-13.97, -2.55) * mm, "end": v(-14.1, -2.33) * mm});
            skLineSegment(sketch, "E169.MirrorCS", {"start": v(-0.76, -2.55) * mm, "end": v(-0.89, -2.33) * mm});
            skLineSegment(sketch, "E170.MirrorCS", {"start": v(-20.07, -2.55) * mm, "end": v(-20.2, -2.33) * mm});
            skLineSegment(sketch, "E171.MirrorCS", {"start": v(-11.3, -2.33) * mm, "end": v(-11.43, -2.55) * mm});
            skLineSegment(sketch, "E172.MirrorCS", {"start": v(-17.27, -2.55) * mm, "end": v(-17.4, -2.33) * mm});
            skLineSegment(sketch, "E173.MirrorCS", {"start": v(-19.56, -2.55) * mm, "end": v(-19.69, -2.33) * mm});
            skLineSegment(sketch, "E174.MirrorCS", {"start": v(-23.75, -2.33) * mm, "end": v(-23.88, -2.55) * mm});
            skLineSegment(sketch, "E175.MirrorCS", {"start": v(-16, -2.55) * mm, "end": v(-16.13, -2.33) * mm});
            skLineSegment(sketch, "E176.MirrorCS", {"start": v(-18.42, -2.33) * mm, "end": v(-18.54, -2.55) * mm});
            skLineSegment(sketch, "E177.MirrorCS", {"start": v(-6.73, -2.33) * mm, "end": v(-6.86, -2.55) * mm});
            skLineSegment(sketch, "E178.MirrorCS", {"start": v(-11.18, -2.55) * mm, "end": v(-11.3, -2.33) * mm});
            skLineSegment(sketch, "E179.MirrorCS", {"start": v(-7.24, -2.33) * mm, "end": v(-7.37, -2.55) * mm});
            skLineSegment(sketch, "E180.MirrorCS", {"start": v(-22.48, -2.33) * mm, "end": v(-22.6, -2.55) * mm});
            skLineSegment(sketch, "E181.MirrorCS", {"start": v(-12.45, -2.55) * mm, "end": v(-12.57, -2.33) * mm});
            skLineSegment(sketch, "E182.MirrorCS", {"start": v(-5.84, -2.55) * mm, "end": v(-5.97, -2.33) * mm});
            skLineSegment(sketch, "E183.MirrorCS", {"start": v(-12.07, -2.33) * mm, "end": v(-12.2, -2.55) * mm});
            skLineSegment(sketch, "E184.MirrorCS", {"start": v(-21.08, -2.55) * mm, "end": v(-21.2, -2.33) * mm});
            skLineSegment(sketch, "E185.MirrorCS", {"start": v(-10.54, -2.33) * mm, "end": v(-10.67, -2.55) * mm});
            skLineSegment(sketch, "E186.MirrorCS", {"start": v(-25.27, -2.33) * mm, "end": v(-25.4, -2.55) * mm});
            skLineSegment(sketch, "E187.MirrorCS", {"start": v(-24.64, -2.55) * mm, "end": v(-24.77, -2.33) * mm});
            skLineSegment(sketch, "E188.MirrorCS", {"start": v(-8.38, -2.55) * mm, "end": v(-8.5, -2.33) * mm});
            skLineSegment(sketch, "E189.MirrorCS", {"start": v(-5.72, -2.33) * mm, "end": v(-5.84, -2.55) * mm});
            skLineSegment(sketch, "E190.MirrorCS", {"start": v(-6.6, -2.55) * mm, "end": v(-6.73, -2.33) * mm});
            skLineSegment(sketch, "E191.MirrorCS", {"start": v(-10.67, -2.55) * mm, "end": v(-10.8, -2.33) * mm});
            skLineSegment(sketch, "E192.MirrorCS", {"start": v(-16.51, -2.55) * mm, "end": v(-16.64, -2.33) * mm});
            skLineSegment(sketch, "E193.MirrorCS", {"start": v(-14.6, -2.33) * mm, "end": v(-14.73, -2.55) * mm});
            skLineSegment(sketch, "E194.MirrorCS", {"start": v(-2.03, -2.55) * mm, "end": v(-2.16, -2.33) * mm});
            skLineSegment(sketch, "E195.MirrorCS", {"start": v(-6.22, -2.33) * mm, "end": v(-6.35, -2.55) * mm});
            skLineSegment(sketch, "E196.MirrorCS", {"start": v(-10.41, -2.55) * mm, "end": v(-10.54, -2.33) * mm});
            skLineSegment(sketch, "E197.MirrorCS", {"start": v(-0.64, -2.33) * mm, "end": v(-0.76, -2.55) * mm});
            skLineSegment(sketch, "E198.MirrorCS", {"start": v(-7.62, -2.55) * mm, "end": v(-7.75, -2.33) * mm});
            skLineSegment(sketch, "E199.MirrorCS", {"start": v(-17.53, -2.55) * mm, "end": v(-17.65, -2.33) * mm});
            skLineSegment(sketch, "E200.MirrorCS", {"start": v(-3.81, -2.55) * mm, "end": v(-3.94, -2.33) * mm});
            skLineSegment(sketch, "E201.MirrorCS", {"start": v(-25.02, -2.33) * mm, "end": v(-25.15, -2.55) * mm});
            skLineSegment(sketch, "E202.MirrorCS", {"start": v(-24.26, -2.33) * mm, "end": v(-24.38, -2.55) * mm});
            skLineSegment(sketch, "E203.MirrorCS", {"start": v(-13.2, -2.55) * mm, "end": v(-13.34, -2.33) * mm});
            skLineSegment(sketch, "E204.MirrorCS", {"start": v(-24.13, -2.55) * mm, "end": v(-24.26, -2.33) * mm});
            skLineSegment(sketch, "E205.MirrorCS", {"start": v(-12.95, -2.55) * mm, "end": v(-13.08, -2.33) * mm});
            skLineSegment(sketch, "E206.MirrorCS", {"start": v(-14.22, -2.55) * mm, "end": v(-14.35, -2.33) * mm});
            skLineSegment(sketch, "E207.MirrorCS", {"start": v(-7.87, -2.55) * mm, "end": v(-8, -2.33) * mm});
            skLineSegment(sketch, "E208.MirrorCS", {"start": v(-11.56, -2.33) * mm, "end": v(-11.68, -2.55) * mm});
            skLineSegment(sketch, "E209.MirrorCS", {"start": v(-11.81, -2.33) * mm, "end": v(-11.94, -2.55) * mm});
            skLineSegment(sketch, "E210.MirrorCS", {"start": v(-7.75, -2.33) * mm, "end": v(-7.87, -2.55) * mm});
            skLineSegment(sketch, "E211.MirrorCS", {"start": v(-22.35, -2.55) * mm, "end": v(-22.48, -2.33) * mm});
            skLineSegment(sketch, "E212.MirrorCS", {"start": v(0, -2.6) * mm, "end": v(-25.4, -2.6) * mm});
            skSolve(sketch);
        }
        {
            var Q0;
            Q0 = qSketchRegion(id + "F4", true);
            extrude(context, id + "F5", {"entities" : qUnion([Q0]), "operationType" : NewBodyOperationType.REMOVE, "endBound" : BoundingType.SYMMETRIC, "oppositeDirection" : true, "depth" : 25.4 * mm, "offsetDistance" : 25.4 * mm});
        }
    });
